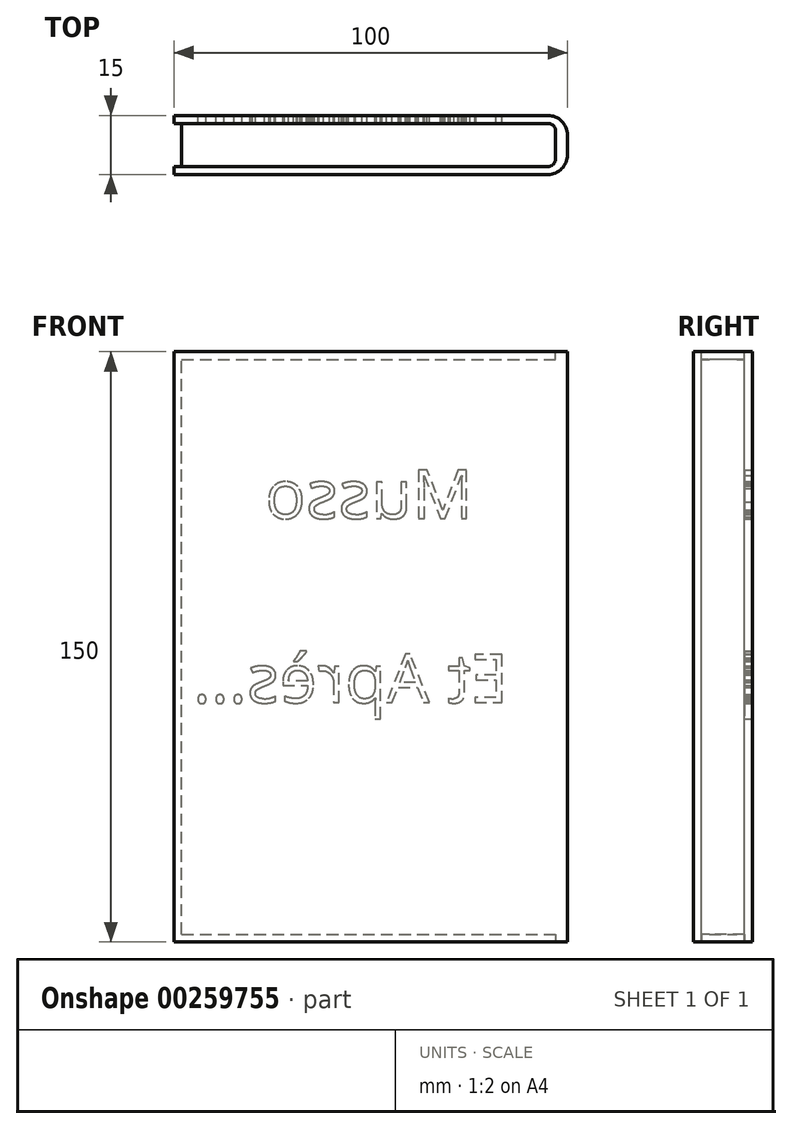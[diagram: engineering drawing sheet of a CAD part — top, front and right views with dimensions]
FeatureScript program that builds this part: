
annotation { "Feature Type Name" : "Feature", "Feature Type Description" : "" }
export const myFeature = defineFeature(function(context is Context, id is Id, definition is map)
    precondition{}
    {
        {
            var Q0;
            Q0=qCreatedBy(makeId("Front.planeOp"),FACE);
            var sketch = newSketch(context, id + "F0", { "sketchPlane" : qUnion([Q0])});
            skLineSegment(sketch, "E0.bottom", {"start": v(-58.67, 80.44) * mm, "end": v(41.33, 80.44) * mm});
            skLineSegment(sketch, "E0.top", {"start": v(-58.67, -69.56) * mm, "end": v(41.33, -69.56) * mm});
            skLineSegment(sketch, "E0.left", {"start": v(-58.67, 80.44) * mm, "end": v(-58.67, -69.56) * mm});
            skLineSegment(sketch, "E0.right", {"start": v(41.33, 80.44) * mm, "end": v(41.33, -69.56) * mm});
            skSolve(sketch);
        }
        {
            var Q0;
            Q0=makeQuery(id+"F0.imprint","IMPRINT",FACE,{"disambiguationData":[TD([[makeQuery(id+"F0.imprint","IMPRINT",EDGE,{"derivedFrom":sQuery(id+"F0.wireOp",EDGE,"E0.bottom")}),-1.0]])]});
            extrude(context, id + "F1", {"entities" : qUnion([Q0]), "depth" : 15 * mm});
        }
        {
            var Q0;
            Q0=makeQuery(id+"F1.opExtrude","CAP_EDGE",EDGE,{"disambiguationData":[OSD([sQuery(id+"F0.wireOp",EDGE,"E0.right")])],"isStart":false});
            var Q1;
            Q1=makeQuery(id+"F1.opExtrude","CAP_EDGE",EDGE,{"disambiguationData":[OSD([sQuery(id+"F0.wireOp",EDGE,"E0.right")])],"isStart":true});
            fillet(context, id + "F2", {"entities" : qUnion([Q0, Q1]), "radius" : 5 * mm, "tangentPropagation" : true, "allowEdgeOverflow" : false});
        }
        {
            var Q0;
            Q0=makeQuery(id+"F1.opExtrude","SWEPT_FACE",FACE,{"disambiguationData":[OSD([sQuery(id+"F0.wireOp",EDGE,"E0.bottom")])]});
            var sketch = newSketch(context, id + "F3", { "sketchPlane" : qUnion([Q0])});
            skLineSegment(sketch, "E1.bottom", {"start": v(-58.67, -2) * mm, "end": v(38.33, -2) * mm});
            skLineSegment(sketch, "E1.top", {"start": v(-58.67, -13) * mm, "end": v(38.33, -13) * mm});
            skLineSegment(sketch, "E1.left", {"start": v(-58.67, -2) * mm, "end": v(-58.67, -13) * mm});
            skLineSegment(sketch, "E1.right", {"start": v(38.33, -2) * mm, "end": v(38.33, -13) * mm});
            skSolve(sketch);
        }
        {
            var Q0;
            Q0=makeQuery(id+"F3.imprint","IMPRINT",FACE,{"disambiguationData":[TD([[makeQuery(id+"F3.imprint","IMPRINT",EDGE,{"derivedFrom":sQuery(id+"F3.wireOp",EDGE,"E1.bottom")}),-1.0]])]});
            extrude(context, id + "F4", {"entities" : qUnion([Q0]), "operationType" : NewBodyOperationType.REMOVE, "oppositeDirection" : true, "depth" : 2 * mm});
        }
        {
            var Q0;
            Q0=makeQuery(id+"F4.boolean.opBoolean","COPY",FACE,{"derivedFrom":makeQuery(id+"F4.opExtrude","CAP_FACE",FACE,{"disambiguationData":[OSD([sQuery(id+"F3.wireOp",EDGE,"E1.bottom"),sQuery(id+"F3.wireOp",EDGE,"E1.top"),sQuery(id+"F3.wireOp",EDGE,"E1.left"),sQuery(id+"F3.wireOp",EDGE,"E1.right")])],"isStart":false})});
            var sketch = newSketch(context, id + "F5", { "sketchPlane" : qUnion([Q0])});
            skLineSegment(sketch, "E2.bottom", {"start": v(-58.67, -2) * mm, "end": v(-56.67, -2) * mm});
            skLineSegment(sketch, "E2.top", {"start": v(-58.67, -13) * mm, "end": v(-56.67, -13) * mm});
            skLineSegment(sketch, "E2.left", {"start": v(-58.67, -2) * mm, "end": v(-58.67, -13) * mm});
            skLineSegment(sketch, "E2.right", {"start": v(-56.67, -2) * mm, "end": v(-56.67, -13) * mm});
            skSolve(sketch);
        }
        {
            var Q0;
            Q0=makeQuery(id+"F5.imprint","IMPRINT",FACE,{"disambiguationData":[TD([[makeQuery(id+"F5.imprint","IMPRINT",EDGE,{"derivedFrom":sQuery(id+"F5.wireOp",EDGE,"E2.bottom")}),-1.0]])]});
            extrude(context, id + "F6", {"entities" : qUnion([Q0]), "operationType" : NewBodyOperationType.REMOVE, "endBound" : BoundingType.THROUGH_ALL, "oppositeDirection" : true, "depth" : 25 * mm});
        }
        {
            var Q0;
            Q0=makeQuery(id+"F1.opExtrude","SWEPT_FACE",FACE,{"disambiguationData":[OSD([sQuery(id+"F0.wireOp",EDGE,"E0.top")])]});
            var sketch = newSketch(context, id + "F7", { "sketchPlane" : qUnion([Q0])});
            skLineSegment(sketch, "E3.bottom", {"start": v(-56.67, 13) * mm, "end": v(38.33, 13) * mm});
            skLineSegment(sketch, "E3.top", {"start": v(-56.67, 2) * mm, "end": v(38.33, 2) * mm});
            skLineSegment(sketch, "E3.left", {"start": v(-56.67, 13) * mm, "end": v(-56.67, 2) * mm});
            skLineSegment(sketch, "E3.right", {"start": v(38.33, 13) * mm, "end": v(38.33, 2) * mm});
            skSolve(sketch);
        }
        {
            var Q0;
            Q0=makeQuery(id+"F7.imprint","IMPRINT",FACE,{"disambiguationData":[TD([[makeQuery(id+"F7.imprint","IMPRINT",EDGE,{"derivedFrom":sQuery(id+"F7.wireOp",EDGE,"E3.bottom")}),-1.0]])]});
            extrude(context, id + "F8", {"entities" : qUnion([Q0]), "operationType" : NewBodyOperationType.REMOVE, "oppositeDirection" : true, "depth" : 2 * mm});
        }
        {
            var Q0;
            Q0=makeQuery(id+"F8.boolean.opBoolean","COPY",EDGE,{"derivedFrom":makeQuery(id+"F8.opExtrude","SWEPT_EDGE",EDGE,{"disambiguationData":[OSD([sQuery(id+"F7.wireOp",EDGE,"E3.bottom"),sQuery(id+"F7.wireOp",EDGE,"E3.right")])]})});
            var Q1;
            Q1=makeQuery(id+"F8.boolean.opBoolean","COPY",EDGE,{"derivedFrom":makeQuery(id+"F8.opExtrude","SWEPT_EDGE",EDGE,{"disambiguationData":[OSD([sQuery(id+"F7.wireOp",EDGE,"E3.top"),sQuery(id+"F7.wireOp",EDGE,"E3.right")])]})});
            var Q2;
            Q2=makeQuery(id+"F4.boolean.opBoolean","COPY",EDGE,{"derivedFrom":makeQuery(id+"F4.opExtrude","SWEPT_EDGE",EDGE,{"disambiguationData":[OSD([sQuery(id+"F3.wireOp",EDGE,"E1.bottom"),sQuery(id+"F3.wireOp",EDGE,"E1.right")])]})});
            var Q3;
            Q3=makeQuery(id+"F4.boolean.opBoolean","COPY",EDGE,{"derivedFrom":makeQuery(id+"F4.opExtrude","SWEPT_EDGE",EDGE,{"disambiguationData":[OSD([sQuery(id+"F3.wireOp",EDGE,"E1.top"),sQuery(id+"F3.wireOp",EDGE,"E1.right")])]})});
            fillet(context, id + "F9", {"entities" : qUnion([Q0, Q1, Q2, Q3]), "radius" : 2 * mm, "tangentPropagation" : true, "allowEdgeOverflow" : false});
        }
        {
            var Q0;
            Q0=makeQuery(id+"F1.opExtrude","CAP_FACE",FACE,{"disambiguationData":[OSD([sQuery(id+"F0.wireOp",EDGE,"E0.bottom"),sQuery(id+"F0.wireOp",EDGE,"E0.top"),sQuery(id+"F0.wireOp",EDGE,"E0.left"),sQuery(id+"F0.wireOp",EDGE,"E0.right")])],"isStart":true});
            var sketch = newSketch(context, id + "F10", { "sketchPlane" : qUnion([Q0])});
            skText(sketch, "E4", { "text": "  Musso\n\nEt Après...", "fontName": "OpenSans-Regular.ttf"});
            const initialGuessF10  = {"E4": [-0.02633, 0.03806, 1, 0, 0.01239]};
            skSetInitialGuess(sketch, initialGuessF10);
            skSolve(sketch);
        }
        {
            var Q0;
            Q0 = qSketchRegion(id + "F10", true);
            extrude(context, id + "F11", {"entities" : qUnion([Q0]), "operationType" : NewBodyOperationType.REMOVE, "oppositeDirection" : true, "depth" : 2 * mm});
        }
    });
